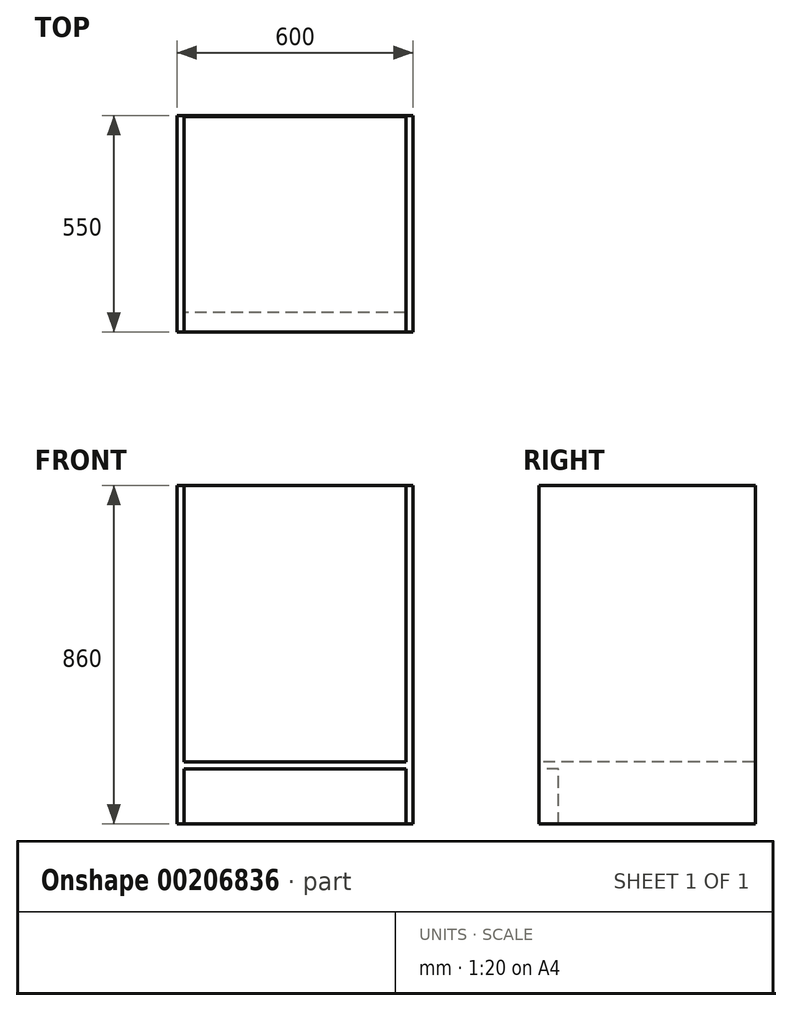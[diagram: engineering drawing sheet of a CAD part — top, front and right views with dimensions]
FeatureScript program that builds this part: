
annotation { "Feature Type Name" : "Feature", "Feature Type Description" : "" }
export const myFeature = defineFeature(function(context is Context, id is Id, definition is map)
    precondition{}
    {
        {
            var Q0;
            Q0=qCreatedBy(makeId("Top.planeOp"),FACE);
            var sketch = newSketch(context, id + "F0", { "sketchPlane" : qUnion([Q0])});
            skLineSegment(sketch, "E0.bottom", {"start": v(-518.83, 504.1) * mm, "end": v(81.17, 504.1) * mm});
            skLineSegment(sketch, "E0.top", {"start": v(-518.83, -45.9) * mm, "end": v(-500.83, -45.9) * mm});
            skLineSegment(sketch, "E0.left", {"start": v(-518.83, 504.1) * mm, "end": v(-518.83, -45.9) * mm});
            skLineSegment(sketch, "E0.right", {"start": v(81.17, 504.1) * mm, "end": v(81.17, -45.9) * mm});
            skLineSegment(sketch, "E1.bottom", {"start": v(-500.83, 501.1) * mm, "end": v(63.17, 501.1) * mm});
            skLineSegment(sketch, "E1.left", {"start": v(-500.83, 501.1) * mm, "end": v(-500.83, -45.9) * mm});
            skLineSegment(sketch, "E1.right", {"start": v(63.17, 501.1) * mm, "end": v(63.17, -45.9) * mm});
            skLineSegment(sketch, "E2.trimOffspring", {"start": v(63.17, -45.9) * mm, "end": v(81.17, -45.9) * mm});
            skSolve(sketch);
        }
        {
            var Q0;
            Q0=qCreatedBy(makeId("Top.planeOp"),FACE);
            var sketch = newSketch(context, id + "F1", { "sketchPlane" : qUnion([Q0])});
            skPoint(sketch, "E3.0", {"position": v(-518.83, 504.1) * mm});
            skLineSegment(sketch, "E4.0", {"start": v(-518.83, 504.1) * mm, "end": v(-518.83, -45.9) * mm});
            skLineSegment(sketch, "E5.0", {"start": v(-518.83, 504.1) * mm, "end": v(81.17, 504.1) * mm});
            skLineSegment(sketch, "E6.0", {"start": v(81.17, 504.1) * mm, "end": v(81.17, -45.9) * mm});
            skLineSegment(sketch, "E7", {"start": v(-518.83, -45.9) * mm, "end": v(81.17, -45.9) * mm});
            skSolve(sketch);
        }
        {
            var Q0;
            Q0=qSketchRegion(id+"F0",true);
            extrude(context, id + "F2", {"entities" : qUnion([Q0]), "depth" : 720 * mm});
        }
        {
            var Q0;
            Q0=qSketchRegion(id+"F1",true);
            extrude(context, id + "F3", {"entities" : qUnion([Q0]), "operationType" : NewBodyOperationType.ADD, "depth" : 18 * mm});
        }
        {
            var Q0;
            Q0=qCreatedBy(makeId("Top.planeOp"),FACE);
            var sketch = newSketch(context, id + "F4", { "sketchPlane" : qUnion([Q0])});
            skLineSegment(sketch, "E8.0", {"start": v(-518.83, 504.1) * mm, "end": v(-518.83, -45.9) * mm});
            skLineSegment(sketch, "E9.0", {"start": v(-518.83, 504.1) * mm, "end": v(81.17, 504.1) * mm});
            skLineSegment(sketch, "E10.0", {"start": v(81.17, 504.1) * mm, "end": v(81.17, -45.9) * mm});
            skLineSegment(sketch, "E11.0", {"start": v(-518.83, -45.9) * mm, "end": v(-500.83, -45.9) * mm});
            skLineSegment(sketch, "E12.0", {"start": v(63.17, -45.9) * mm, "end": v(81.17, -45.9) * mm});
            skLineSegment(sketch, "E13", {"start": v(63.17, -45.9) * mm, "end": v(63.17, 4.1) * mm});
            skLineSegment(sketch, "E14", {"start": v(63.17, 4.1) * mm, "end": v(-500.83, 4.1) * mm});
            skLineSegment(sketch, "E15", {"start": v(-500.83, 4.1) * mm, "end": v(-500.83, -45.9) * mm});
            skSolve(sketch);
        }
        {
            var Q0;
            Q0=qSketchRegion(id+"F4",true);
            extrude(context, id + "F5", {"entities" : qUnion([Q0]), "operationType" : NewBodyOperationType.ADD, "oppositeDirection" : true, "depth" : 140 * mm});
        }
    });
